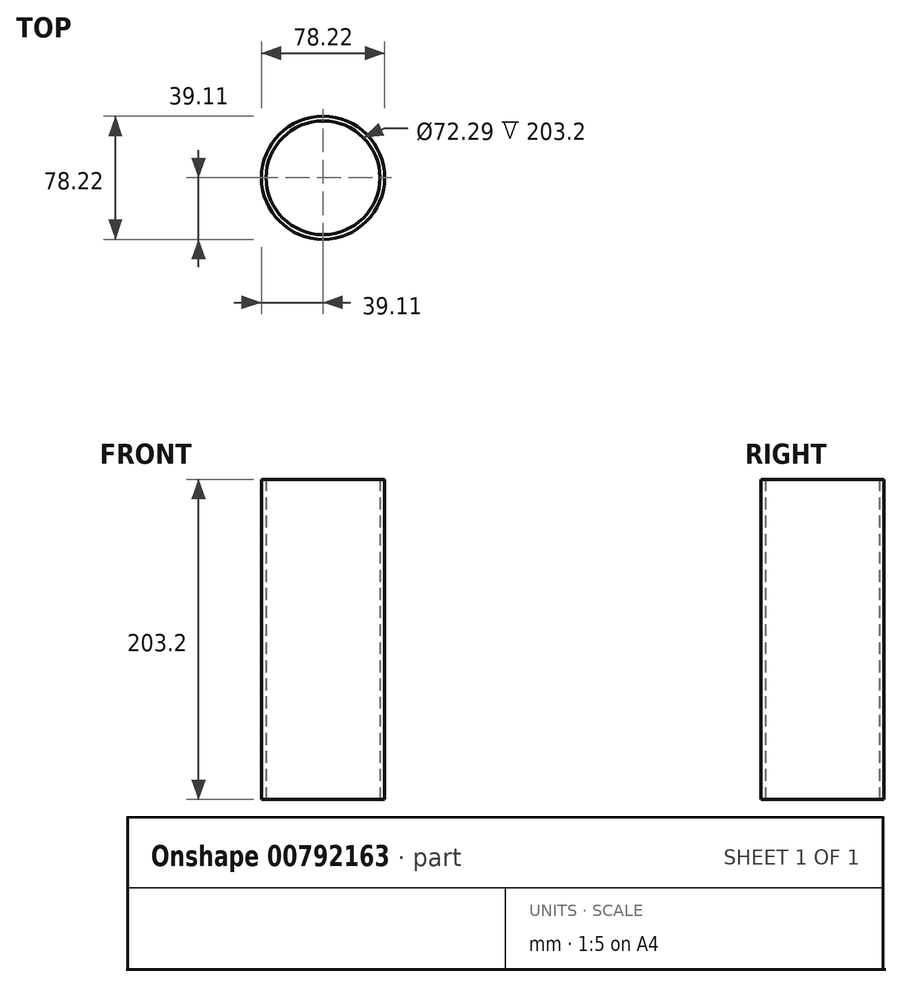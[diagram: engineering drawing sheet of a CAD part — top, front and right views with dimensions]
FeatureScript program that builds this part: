
annotation { "Feature Type Name" : "Feature", "Feature Type Description" : "" }
export const myFeature = defineFeature(function(context is Context, id is Id, definition is map)
    precondition{}
    {
        {
            var Q0;
            Q0=qCreatedBy(makeId("Top.planeOp"),FACE);
            var sketch = newSketch(context, id + "F0", { "sketchPlane" : qUnion([Q0])});
            skCircle(sketch, "E0", {"center": v(0, 0) * mm, "radius": 36.14 * mm});
            skCircle(sketch, "E1", {"center": v(0, 0) * mm, "radius": 39.1 * mm});
            skSolve(sketch);
        }
        {
            var Q0;
            Q0 = qSketchRegion(id + "F0", true);
            extrude(context, id + "F1", {"entities" : qUnion([Q0]), "depth" : 203.2 * mm, "offsetDistance" : 25.4 * mm});
        }
    });
